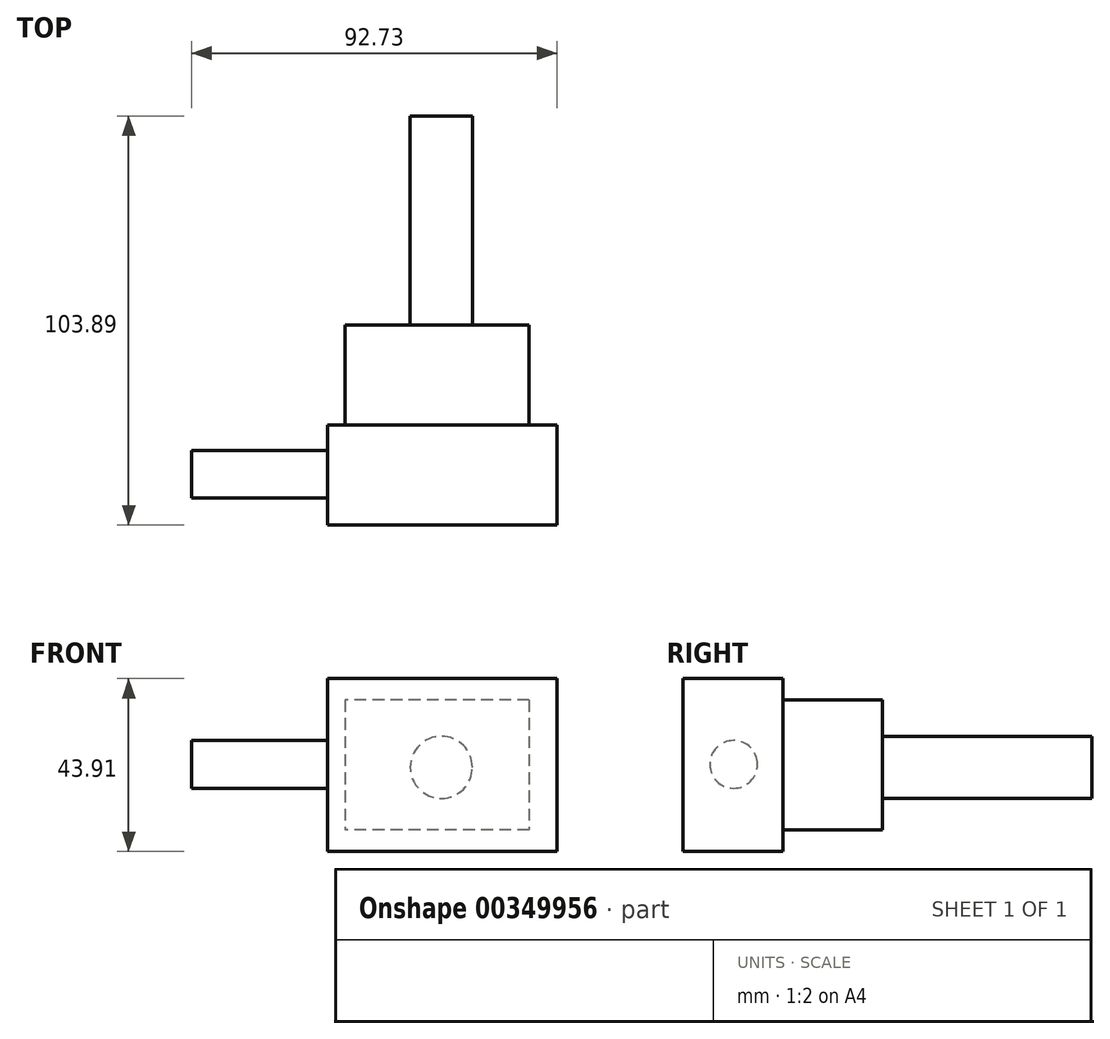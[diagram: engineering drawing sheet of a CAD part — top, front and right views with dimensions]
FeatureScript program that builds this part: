
annotation { "Feature Type Name" : "Feature", "Feature Type Description" : "" }
export const myFeature = defineFeature(function(context is Context, id is Id, definition is map)
    precondition{}
    {
        {
            var Q0;
            Q0=qCreatedBy(makeId("Front.planeOp"),FACE);
            var sketch = newSketch(context, id + "F0", { "sketchPlane" : qUnion([Q0])});
            skLineSegment(sketch, "E0.bottom", {"start": v(-25.98, 15.59) * mm, "end": v(32.21, 15.59) * mm});
            skLineSegment(sketch, "E0.top", {"start": v(-25.98, -28.32) * mm, "end": v(32.21, -28.32) * mm});
            skLineSegment(sketch, "E0.left", {"start": v(-25.98, 15.59) * mm, "end": v(-25.98, -28.32) * mm});
            skLineSegment(sketch, "E0.right", {"start": v(32.21, 15.59) * mm, "end": v(32.21, -28.32) * mm});
            skSolve(sketch);
        }
        {
            var Q0;
            Q0 = qSketchRegion(id + "F0", true);
            extrude(context, id + "F1", {"entities" : qUnion([Q0]), "depth" : 25.4 * mm});
        }
        {
            var Q0;
            Q0=makeQuery(id+"F1.opExtrude","SWEPT_FACE",FACE,{"disambiguationData":[OSD([sQuery(id+"F0.wireOp",EDGE,"E0.left")])]});
            var sketch = newSketch(context, id + "F2", { "sketchPlane" : qUnion([Q0])});
            skCircle(sketch, "E1", {"center": v(12.47, -6.23) * mm, "radius": 6.06 * mm});
            skSolve(sketch);
        }
        {
            var Q0;
            Q0 = qSketchRegion(id + "F2", true);
            extrude(context, id + "F3", {"entities" : qUnion([Q0]), "operationType" : NewBodyOperationType.ADD, "depth" : 34.54 * mm});
        }
        {
            var Q0;
            Q0=makeQuery(id+"F1.opExtrude","CAP_FACE",FACE,{"disambiguationData":[OSD([sQuery(id+"F0.wireOp",EDGE,"E0.bottom"),sQuery(id+"F0.wireOp",EDGE,"E0.top"),sQuery(id+"F0.wireOp",EDGE,"E0.left"),sQuery(id+"F0.wireOp",EDGE,"E0.right")])],"isStart":true});
            var sketch = newSketch(context, id + "F4", { "sketchPlane" : qUnion([Q0])});
            skLineSegment(sketch, "E2.bottom", {"start": v(-25.2, 10.13) * mm, "end": v(21.56, 10.13) * mm});
            skLineSegment(sketch, "E2.top", {"start": v(-25.2, -22.86) * mm, "end": v(21.56, -22.86) * mm});
            skLineSegment(sketch, "E2.left", {"start": v(-25.2, 10.13) * mm, "end": v(-25.2, -22.86) * mm});
            skLineSegment(sketch, "E2.right", {"start": v(21.56, 10.13) * mm, "end": v(21.56, -22.86) * mm});
            skSolve(sketch);
        }
        {
            var Q0;
            Q0 = qSketchRegion(id + "F4", true);
            extrude(context, id + "F5", {"entities" : qUnion([Q0]), "operationType" : NewBodyOperationType.ADD, "depth" : 25.4 * mm});
        }
        {
            var Q0;
            Q0=makeQuery(id+"F5.opExtrude","CAP_FACE",FACE,{"disambiguationData":[OSD([sQuery(id+"F4.wireOp",EDGE,"E2.bottom"),sQuery(id+"F4.wireOp",EDGE,"E2.top"),sQuery(id+"F4.wireOp",EDGE,"E2.left"),sQuery(id+"F4.wireOp",EDGE,"E2.right")])],"isStart":false});
            var sketch = newSketch(context, id + "F6", { "sketchPlane" : qUnion([Q0])});
            skCircle(sketch, "E3", {"center": v(-2.88, -6.97) * mm, "radius": 7.9 * mm});
            skSolve(sketch);
        }
        {
            var Q0;
            Q0 = qSketchRegion(id + "F6", true);
            extrude(context, id + "F7", {"entities" : qUnion([Q0]), "operationType" : NewBodyOperationType.ADD, "depth" : 53.1 * mm});
        }
    });
